# Revit family: Single Skin Roofing_Brownie Blanket (STC 29_Uvalue 0.60)
name_source: partatom
category: Generic Models
units: mm (PartAtom-declared; Revit-internal decimal feet)

## family parameters
Can host rebar = No
Cut with Voids When Loaded = No
Host = Face
Part Type = Normal
Room Calculation Point = No
Round Connector Dimension = Use Diameter
Shared = No

## types (2) — shared parameters
Actual Width (mm) = 3000 mm  [stored 9.84252 ft]
Aluminium foil = Aluminium foil (Double Sided)
ArrayNum = 3
ArrayNum (Top Skin) = 9
Description = ECOWOOL Brownie blanket and slabs are resilient, non-combustible, glass mineral wool products, supplied at roofing and walling application for residential and commercial building
Insulation = BROWNIE BLANKET
Insulation Density = 32 kg/m³
Insulation Density (kg/m3) = 32 mm  [stored 0.104987 ft]
Insulation thk. (mm) = 50 mm  [stored 0.164042 ft]
Length (mm) = 2000 mm  [stored 6.56168 ft]
Length Insulation = 2000 mm  [stored 6.56168 ft]
Manufacturer = PGF Insulation Sdn. Bhd.
ProVisSingle (Top Skin) = No
ProfArrN = 3
ProfArrN (Top Skin) = 9
ProfVisDouble = Yes
ProfVisDouble (Top Skin) = Yes
ProfVisSingle = No
SubL = 2805 mm  [stored 9.20276 ft]
SubL (Top Skin) = 2718 mm  [stored 8.91732 ft]
SubW = 3740 mm
SubW (Top Skin) = 3020 mm  [stored 9.90814 ft]
Thermal K Value = 0.0327
Thermal R Value = 1.5
Type of Insulation = Glass Mineral Wool Blanket
URL = www.ecowool.com.my
zero-valued in all types: Default Elevation

## per-type parameters (varying)
| type | A | ECOWOOL Product thickness in mm | Finish | Remarks | STC in dB | System Description | Total System Thickness-mm | Typical weight of ECOWOOL-Kg/M2 | U-Value W/m2k |
| ECOWOOL EWBL1.50 | 76.5 mm  [stored 0.250984 ft] | 50  x 32 Kg/m3 | Metal Deck Roofing | Single skin metal roof for food centre
or canteen, low cost warehouses, usually non air-condition,
without walls and highly ventilated
environment. Also commonly used
in walkways and common pavilion
in residential estates | 29 | 1. Aluminum Foil
2. Ecowool  EWBL1.45
3. Metal Deck/ Zincalume Liner | 52.95 mm  [stored 0.17372 ft] | 1.6 mm  [stored 0.00524934 ft] | 0.6 mm  [stored 0.0019685 ft] |
| 50mm | 51.5 mm  [stored 0.168963 ft] |  | ZINCALUME® ULTRA -  ACTIVATE™ |  | 0 |  | 0 mm  [stored 0 ft] | 0 mm  [stored 0 ft] | 0 mm  [stored 0 ft] |

note: [stored X ft] marks values corroborated as IEEE doubles in the binary element streams (Revit-internal decimal feet)

## geometry (parser evidence)
native form markers: Sweep x26
no freeform markers — native parametric forms only
